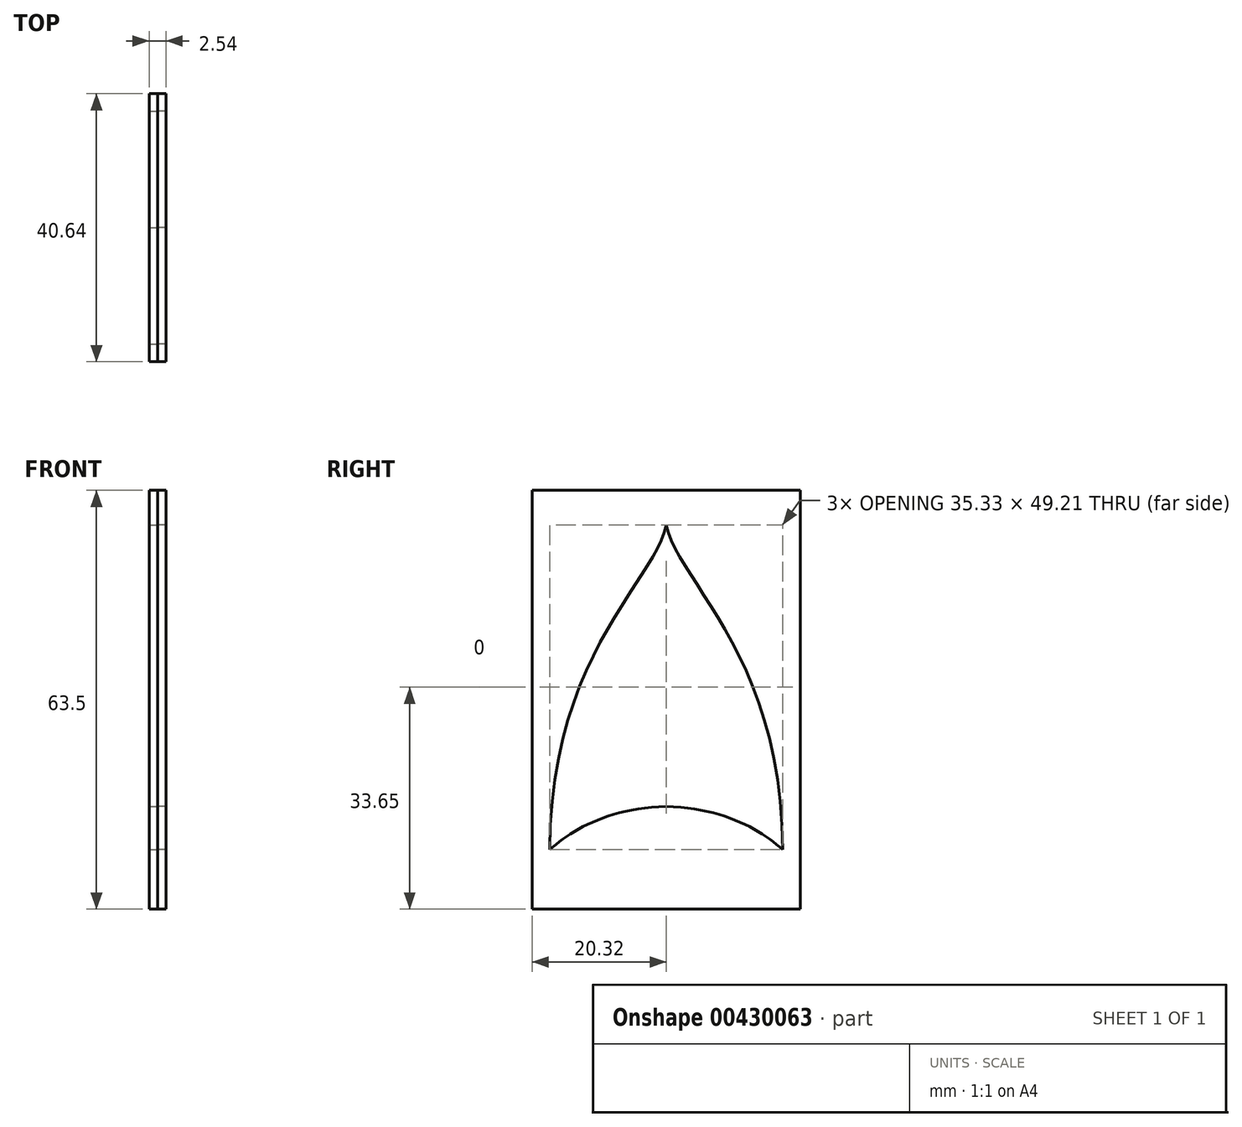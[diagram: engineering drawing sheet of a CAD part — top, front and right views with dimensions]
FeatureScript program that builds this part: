
annotation { "Feature Type Name" : "Feature", "Feature Type Description" : "" }
export const myFeature = defineFeature(function(context is Context, id is Id, definition is map)
    precondition{}
    {
        {
            var Q0;
            Q0=qCreatedBy(makeId("Right.planeOp"),FACE);
            var sketch = newSketch(context, id + "F0", { "sketchPlane" : qUnion([Q0])});
            skLineSegment(sketch, "E0.bottom", {"start": v(-20.32, 38.34) * mm, "end": v(20.32, 38.34) * mm});
            skLineSegment(sketch, "E0.top", {"start": v(-20.32, -25.16) * mm, "end": v(20.32, -25.16) * mm});
            skLineSegment(sketch, "E0.left", {"start": v(-20.32, 38.34) * mm, "end": v(-20.32, -25.16) * mm});
            skLineSegment(sketch, "E0.right", {"start": v(20.32, 38.34) * mm, "end": v(20.32, -25.16) * mm});
            skFitSpline(sketch, "E1", {"points": [v(0, 33.1) * mm, v(17.66, -16.12) * mm], "startDerivative": vector(5.38, -26.03) * mm, "endDerivative": vector(0.4, -88.44) * mm});
            skFitSpline(sketch, "E2.MirrorCS", {"points": [v(0, 33.1) * mm, v(-17.66, -16.12) * mm], "startDerivative": vector(-5.38, -26.03) * mm, "endDerivative": vector(-0.4, -88.44) * mm});
            skFitSpline(sketch, "E3", {"points": [v(-17.66, -16.12) * mm, v(0, -9.56) * mm], "startDerivative": vector(10.27, 9.04) * mm, "endDerivative": vector(26.16, 0.79) * mm});
            skFitSpline(sketch, "E4.MirrorCS", {"points": [v(17.66, -16.12) * mm, v(0, -9.56) * mm], "startDerivative": vector(-10.27, 9.04) * mm, "endDerivative": vector(-26.16, 0.79) * mm});
            skSolve(sketch);
        }
        {
            var Q0;
            Q0=makeQuery(id+"F0.imprint","IMPRINT",FACE,{"disambiguationData":[TD([[makeQuery(id+"F0.imprint","IMPRINT",EDGE,{"derivedFrom":sQuery(id+"F0.wireOp",EDGE,"E0.bottom")}),-1.0]])]});
            extrude(context, id + "F1", {"entities" : qUnion([Q0]), "depth" : 1.27 * mm});
        }
        {
            var Q0;
            Q0 = qSketchRegion(id + "F0", true);
            var Q1;
            Q1=makeQuery(id+"F1.opExtrude","CAP_FACE",FACE,{"disambiguationData":[OSD([sQuery(id+"F0.wireOp",EDGE,"E0.bottom"),sQuery(id+"F0.wireOp",EDGE,"E0.top"),sQuery(id+"F0.wireOp",EDGE,"E0.left"),sQuery(id+"F0.wireOp",EDGE,"E0.right"),sQuery(id+"F0.wireOp",EDGE,"E1"),sQuery(id+"F0.wireOp",EDGE,"E2.MirrorCS"),sQuery(id+"F0.wireOp",EDGE,"E3"),sQuery(id+"F0.wireOp",EDGE,"E4.MirrorCS")])],"isStart":true});
            extrude(context, id + "F2", {"entities" : qUnion([Q0, Q1]), "oppositeDirection" : true, "depth" : 1.27 * mm});
        }
    });
